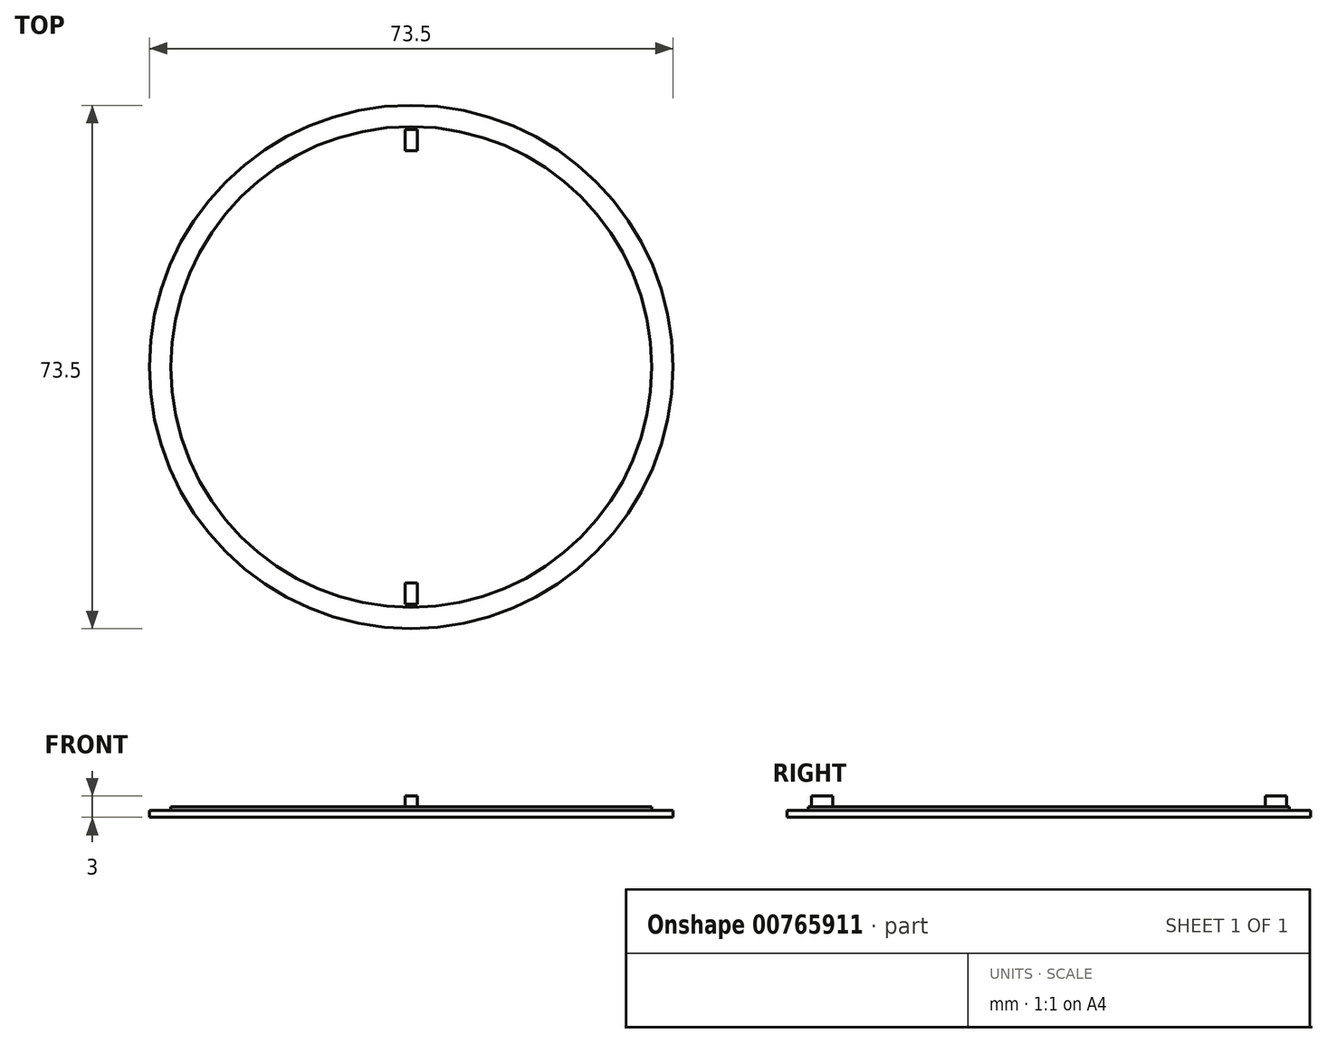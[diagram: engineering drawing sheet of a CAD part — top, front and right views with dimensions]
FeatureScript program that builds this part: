
annotation { "Feature Type Name" : "Feature", "Feature Type Description" : "" }
export const myFeature = defineFeature(function(context is Context, id is Id, definition is map)
    precondition{}
    {
        {
            var Q0;
            Q0=qCreatedBy(makeId("Top.planeOp"),FACE);
            var sketch = newSketch(context, id + "F0", { "sketchPlane" : qUnion([Q0])});
            skCircle(sketch, "E0", {"center": v(0, 0) * mm, "radius": 36.75 * mm});
            skSolve(sketch);
        }
        {
            var Q0;
            Q0=makeQuery(id+"F0.imprint","IMPRINT",FACE,{"disambiguationData":[TD([[makeQuery(id+"F0.imprint","IMPRINT",EDGE,{"derivedFrom":sQuery(id+"F0.wireOp",EDGE,"E0")}),1.0]])]});
            extrude(context, id + "F1", {"entities" : qUnion([Q0]), "depth" : 1 * mm, "offsetDistance" : 25 * mm});
        }
        {
            var Q0;
            Q0=makeQuery(id+"F1.opExtrude","CAP_FACE",FACE,{"disambiguationData":[OSD([sQuery(id+"F0.wireOp",EDGE,"E0")])],"isStart":false});
            var sketch = newSketch(context, id + "F2", { "sketchPlane" : qUnion([Q0])});
            skCircle(sketch, "E1", {"center": v(0, 0) * mm, "radius": 33.75 * mm});
            skLineSegment(sketch, "E2.bottom", {"start": v(0.85, 33.35) * mm, "end": v(-0.85, 33.35) * mm});
            skLineSegment(sketch, "E2.top", {"start": v(0.85, 30.35) * mm, "end": v(-0.85, 30.35) * mm});
            skLineSegment(sketch, "E2.left", {"start": v(0.85, 33.35) * mm, "end": v(0.85, 30.35) * mm});
            skLineSegment(sketch, "E2.right", {"start": v(-0.85, 33.35) * mm, "end": v(-0.85, 30.35) * mm});
            skPoint(sketch, "E2.middle", {"position": v(0, 31.85) * mm});
            skLineSegment(sketch, "E3.MirrorCS", {"start": v(-0.85, -33.35) * mm, "end": v(-0.85, -30.35) * mm});
            skLineSegment(sketch, "E4.MirrorCS", {"start": v(0.85, -30.35) * mm, "end": v(-0.85, -30.35) * mm});
            skPoint(sketch, "E5.MirrorP", {"position": v(0, -31.85) * mm});
            skLineSegment(sketch, "E6.MirrorCS", {"start": v(0.85, -33.35) * mm, "end": v(-0.85, -33.35) * mm});
            skLineSegment(sketch, "E7.MirrorCS", {"start": v(0.85, -33.35) * mm, "end": v(0.85, -30.35) * mm});
            skSolve(sketch);
        }
        {
            var Q0;
            Q0=makeQuery(id+"F2.imprint","IMPRINT",FACE,{"disambiguationData":[TD([[makeQuery(id+"F2.imprint","IMPRINT",EDGE,{"derivedFrom":sQuery(id+"F2.wireOp",EDGE,"E1")}),1.0]])]});
            extrude(context, id + "F3", {"entities" : qUnion([Q0]), "operationType" : NewBodyOperationType.ADD, "depth" : 0.5 * mm, "offsetDistance" : 25 * mm});
        }
        {
            var Q0;
            Q0=makeQuery(id+"F3.boolean.opBoolean","SPLIT",FACE,{"disambiguationData":[TD([makeQuery(id+"F3.opExtrude","SWEPT_FACE",FACE,{"disambiguationData":[OSD([sQuery(id+"F2.wireOp",EDGE,"E3.MirrorCS")])]})])],"derivedFrom":makeQuery(id+"F1.opExtrude","CAP_FACE",FACE,{"disambiguationData":[OSD([sQuery(id+"F0.wireOp",EDGE,"E0")])],"isStart":false})});
            var Q1;
            Q1=makeQuery(id+"F3.boolean.opBoolean","SPLIT",FACE,{"disambiguationData":[TD([makeQuery(id+"F3.opExtrude","SWEPT_FACE",FACE,{"disambiguationData":[OSD([sQuery(id+"F2.wireOp",EDGE,"E2.bottom")])]})])],"derivedFrom":makeQuery(id+"F1.opExtrude","CAP_FACE",FACE,{"disambiguationData":[OSD([sQuery(id+"F0.wireOp",EDGE,"E0")])],"isStart":false})});
            extrude(context, id + "F4", {"entities" : qUnion([Q0, Q1]), "operationType" : NewBodyOperationType.ADD, "depth" : 2 * mm, "offsetDistance" : 25 * mm});
        }
    });
